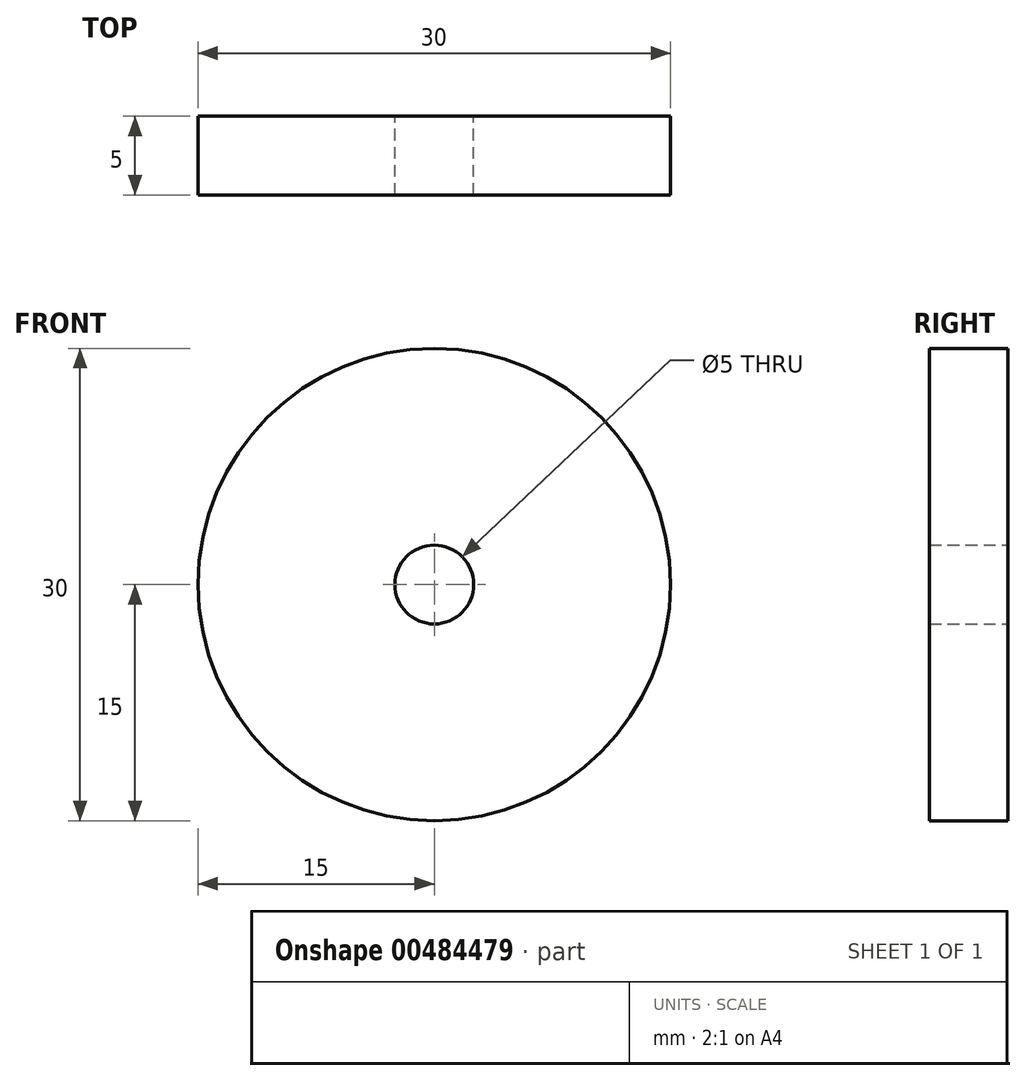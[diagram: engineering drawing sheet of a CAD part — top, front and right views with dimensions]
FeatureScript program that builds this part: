
annotation { "Feature Type Name" : "Feature", "Feature Type Description" : "" }
export const myFeature = defineFeature(function(context is Context, id is Id, definition is map)
    precondition{}
    {
        {
            var Q0;
            Q0=qCreatedBy(makeId("Front.planeOp"),FACE);
            var sketch = newSketch(context, id + "F0", { "sketchPlane" : qUnion([Q0])});
            skCircle(sketch, "E0", {"center": v(0, 0) * mm, "radius": 15 * mm});
            skCircle(sketch, "E1", {"center": v(0, 0) * mm, "radius": 2.5 * mm});
            skSolve(sketch);
        }
        {
            var Q0;
            Q0=makeQuery(id+"F0.imprint","IMPRINT",FACE,{"disambiguationData":[TD([[makeQuery(id+"F0.imprint","IMPRINT",EDGE,{"derivedFrom":sQuery(id+"F0.wireOp",EDGE,"E0")}),1.0]])]});
            var Q1;
            Q1=sQuery(id+"F0.wireOp",EDGE,"E0");
            extrude(context, id + "F1", {"entities" : qUnion([Q0]), "surfaceEntities" : qUnion([Q1]), "depth" : 5 * mm});
        }
    });
